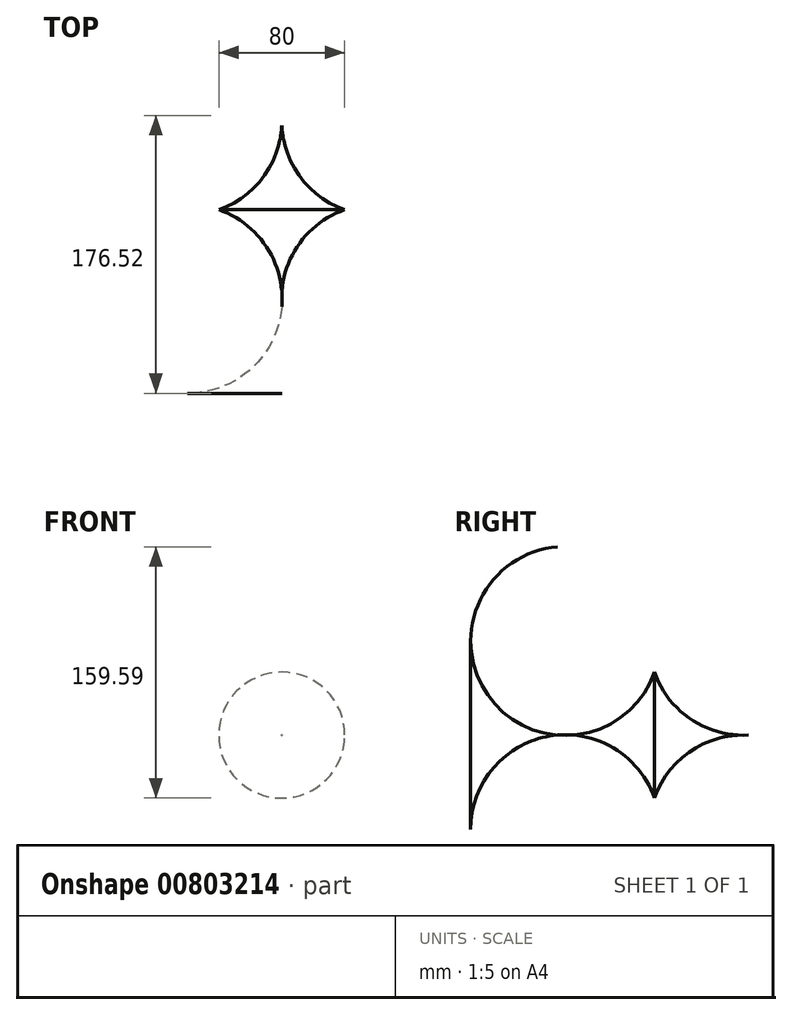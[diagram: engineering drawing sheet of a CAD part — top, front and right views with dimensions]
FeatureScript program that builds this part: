
annotation { "Feature Type Name" : "Feature", "Feature Type Description" : "" }
export const myFeature = defineFeature(function(context is Context, id is Id, definition is map)
    precondition{}
    {
        {
            var Q0;
            Q0=qCreatedBy(makeId("Top.planeOp"),FACE);
            var sketch = newSketch(context, id + "F0", { "sketchPlane" : qUnion([Q0])});
            skLineSegment(sketch, "E0", {"start": v(0, 73.26) * mm, "end": v(0, -73) * mm, "construction": true});
            skArc(sketch, "E1", {"start": v(40, 4.82) * mm, "mid": v(12.35, -15.1) * mm, "end": v(0, -46.85) * mm});
            skArc(sketch, "E2", {"start": v(0, 58.15) * mm, "mid": v(11.91, 25.42) * mm, "end": v(40, 4.82) * mm});
            skLineSegment(sketch, "E3", {"start": v(0, 58.15) * mm, "end": v(0, -46.85) * mm});
            skSolve(sketch);
        }
        {
            var Q0;
            Q0=makeQuery(id+"F0.imprint","IMPRINT",FACE,{"disambiguationData":[TD([[makeQuery(id+"F0.imprint","IMPRINT",EDGE,{"derivedFrom":sQuery(id+"F0.wireOp",EDGE,"E1")}),-1.0]])]});
            var Q1;
            Q1=sQuery(id+"F0.wireOp",EDGE,"E3");
            revolve(context, id + "F1", {"surfaceOperationType" : NewSurfaceOperationType.NEW, "entities" : qUnion([Q0]), "axis" : qUnion([Q1]), "revolveType" : RevolveType.FULL});
        }
    });
